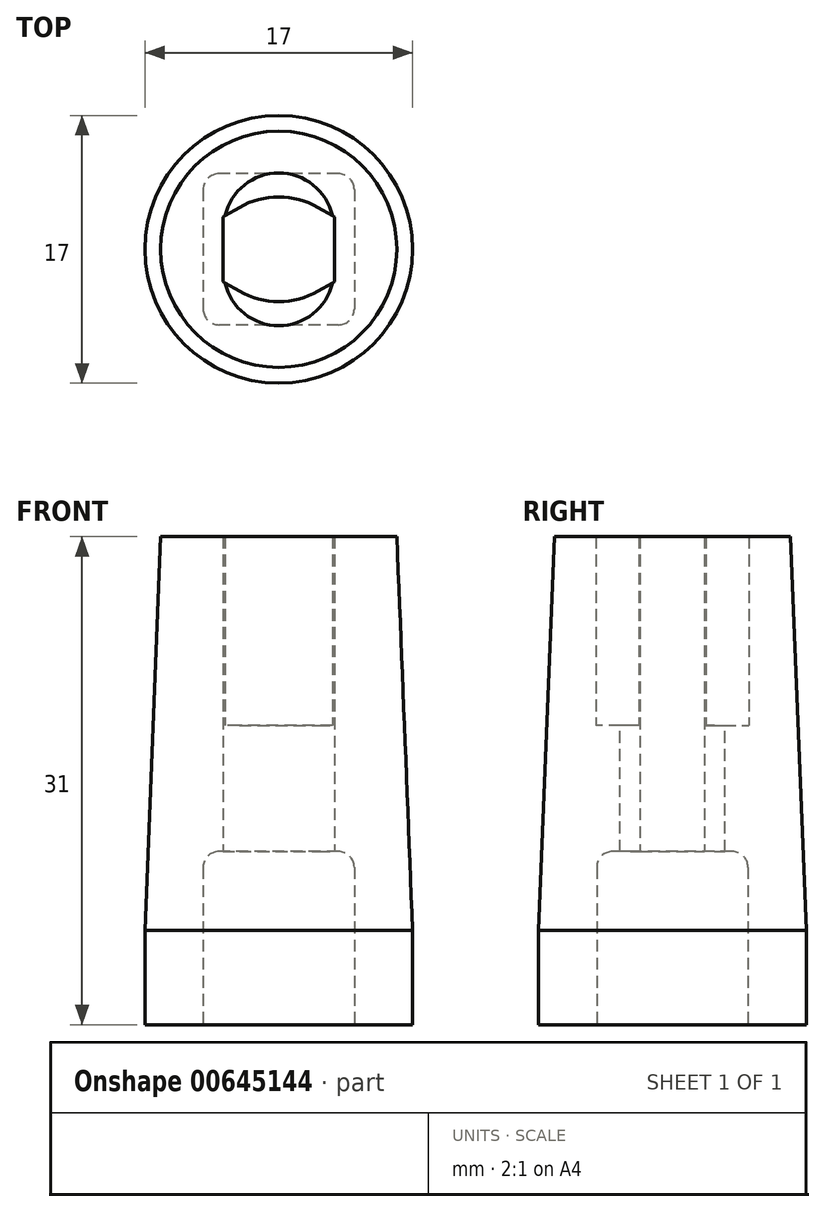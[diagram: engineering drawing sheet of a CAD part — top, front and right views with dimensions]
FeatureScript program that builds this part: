
annotation { "Feature Type Name" : "Feature", "Feature Type Description" : "" }
export const myFeature = defineFeature(function(context is Context, id is Id, definition is map)
    precondition{}
    {
        {
            var Q0;
            Q0=qCreatedBy(makeId("Top.planeOp"),FACE);
            var sketch = newSketch(context, id + "F0", { "sketchPlane" : qUnion([Q0])});
            skCircle(sketch, "E0.cCircle", {"center": v(0, 0) * mm, "radius": 3.55 * mm, "construction": true});
            skLineSegment(sketch, "E0.0", {"start": v(3.55, 2.05) * mm, "end": v(3.55, -2.05) * mm});
            skLineSegment(sketch, "E0.1", {"start": v(3.55, -2.05) * mm, "end": v(0, -4.1) * mm});
            skLineSegment(sketch, "E0.2", {"start": v(0, -4.1) * mm, "end": v(-3.55, -2.05) * mm});
            skLineSegment(sketch, "E0.3", {"start": v(-3.55, -2.05) * mm, "end": v(-3.55, 2.05) * mm});
            skLineSegment(sketch, "E0.4", {"start": v(-3.55, 2.05) * mm, "end": v(0, 4.1) * mm});
            skLineSegment(sketch, "E0.5", {"start": v(0, 4.1) * mm, "end": v(3.55, 2.05) * mm});
            skPoint(sketch, "E0.0.midPoint", {"position": v(3.55, 0) * mm});
            skLineSegment(sketch, "E1.bottom", {"start": v(3.5, 1.35) * mm, "end": v(-3.5, 1.35) * mm, "construction": true});
            skLineSegment(sketch, "E1.top", {"start": v(3.5, -1.35) * mm, "end": v(-3.5, -1.35) * mm, "construction": true});
            skLineSegment(sketch, "E1.left", {"start": v(3.5, 1.35) * mm, "end": v(3.5, -1.35) * mm});
            skLineSegment(sketch, "E1.right", {"start": v(-3.5, 1.35) * mm, "end": v(-3.5, -1.35) * mm});
            skArc(sketch, "E2", {"start": v(3.5, 1.35) * mm, "mid": v(0, 4.85) * mm, "end": v(-3.5, 1.35) * mm});
            skArc(sketch, "E3", {"start": v(-3.5, -1.35) * mm, "mid": v(0, -4.85) * mm, "end": v(3.5, -1.35) * mm});
            skCircle(sketch, "E4", {"center": v(0, 0) * mm, "radius": 8.5 * mm});
            skSolve(sketch);
        }
        {
            var Q0;
            {var subQ5=sQuery(id+"F0.wireOp",EDGE,"E0.0");Q0=makeQuery(id+"F0.imprint","IMPRINT",FACE,{"disambiguationData":[TD([[makeQuery(id+"F0.imprint","IMPRINT",EDGE,{"derivedFrom":subQ5}),1.0]])]});}
            extrude(context, id + "F1", {"entities" : qUnion([Q0]), "depth" : 16 * mm, "offsetDistance" : 25 * mm});
        }
        {
            var Q0;
            {var subQ0=sQuery(id+"F0.wireOp",EDGE,"E0.5");var subQ1=sQuery(id+"F0.wireOp",EDGE,"E0.4");var subQ2=makeQuery(id+"F0.imprint","INTERSECT",VERTEX,{"derivedFrom":[subQ1,subQ0]});Q0=makeQuery(id+"F0.imprint","IMPRINT",FACE,{"disambiguationData":[TD([[makeQuery(id+"F0.imprint","IMPRINT",EDGE,{"disambiguationData":[TD([[subQ2,1.0]])],"derivedFrom":subQ1}),1.0]])]});}
            var Q1;
            {var subQ0=sQuery(id+"F0.wireOp",EDGE,"E0.2");var subQ1=sQuery(id+"F0.wireOp",EDGE,"E0.1");var subQ2=makeQuery(id+"F0.imprint","INTERSECT",VERTEX,{"derivedFrom":[subQ1,subQ0]});Q1=makeQuery(id+"F0.imprint","IMPRINT",FACE,{"disambiguationData":[TD([[makeQuery(id+"F0.imprint","IMPRINT",EDGE,{"disambiguationData":[TD([[subQ2,1.0]])],"derivedFrom":subQ1}),1.0]])]});}
            extrude(context, id + "F2", {"entities" : qUnion([Q0, Q1]), "operationType" : NewBodyOperationType.ADD, "depth" : 4 * mm, "offsetDistance" : 25 * mm});
        }
        {
            var Q0;
            {var subQ5=sQuery(id+"F0.wireOp",EDGE,"E0.0");Q0=makeQuery(id+"F0.imprint","IMPRINT",FACE,{"disambiguationData":[TD([[makeQuery(id+"F0.imprint","IMPRINT",EDGE,{"derivedFrom":subQ5}),1.0]])]});}
            var Q1;
            {var subQ2=sQuery(id+"F0.wireOp",EDGE,"E0.3");Q1=makeQuery(id+"F0.imprint","IMPRINT",FACE,{"disambiguationData":[TD([[makeQuery(id+"F0.imprint","IMPRINT",EDGE,{"derivedFrom":subQ2}),-1.0]])]});}
            var Q2;
            {var subQ0=sQuery(id+"F0.wireOp",EDGE,"E0.5");var subQ1=sQuery(id+"F0.wireOp",EDGE,"E0.4");var subQ2=makeQuery(id+"F0.imprint","INTERSECT",VERTEX,{"derivedFrom":[subQ1,subQ0]});Q2=makeQuery(id+"F0.imprint","IMPRINT",FACE,{"disambiguationData":[TD([[makeQuery(id+"F0.imprint","IMPRINT",EDGE,{"disambiguationData":[TD([[subQ2,1.0]])],"derivedFrom":subQ1}),1.0]])]});}
            var Q3;
            {var subQ0=sQuery(id+"F0.wireOp",EDGE,"E0.2");var subQ1=sQuery(id+"F0.wireOp",EDGE,"E0.1");var subQ2=makeQuery(id+"F0.imprint","INTERSECT",VERTEX,{"derivedFrom":[subQ1,subQ0]});Q3=makeQuery(id+"F0.imprint","IMPRINT",FACE,{"disambiguationData":[TD([[makeQuery(id+"F0.imprint","IMPRINT",EDGE,{"disambiguationData":[TD([[subQ2,1.0]])],"derivedFrom":subQ1}),1.0]])]});}
            var Q4;
            {var subQ1=sQuery(id+"F0.wireOp",EDGE,"E0.0");Q4=makeQuery(id+"F0.imprint","IMPRINT",FACE,{"disambiguationData":[TD([[makeQuery(id+"F0.imprint","IMPRINT",EDGE,{"derivedFrom":subQ1}),-1.0]])]});}
            extrude(context, id + "F3", {"entities" : qUnion([Q0, Q1, Q2, Q3, Q4]), "operationType" : NewBodyOperationType.ADD, "oppositeDirection" : true, "depth" : 15 * mm, "offsetDistance" : 25 * mm});
        }
        {
            var Q0;
            Q0=makeQuery(id+"F3.opExtrude","CAP_FACE",FACE,{"disambiguationData":[OSD([sQuery(id+"F0.wireOp",EDGE,"E4")])],"isStart":false});
            var sketch = newSketch(context, id + "F4", { "sketchPlane" : qUnion([Q0])});
            skLineSegment(sketch, "E5.bottom", {"start": v(4.8, -4.8) * mm, "end": v(-4.8, -4.8) * mm});
            skLineSegment(sketch, "E5.top", {"start": v(4.8, 4.8) * mm, "end": v(-4.8, 4.8) * mm});
            skLineSegment(sketch, "E5.left", {"start": v(4.8, -4.8) * mm, "end": v(4.8, 4.8) * mm});
            skLineSegment(sketch, "E5.right", {"start": v(-4.8, -4.8) * mm, "end": v(-4.8, 4.8) * mm});
            skPoint(sketch, "E5.middle", {"position": v(0, 0) * mm});
            skSolve(sketch);
        }
        {
            var Q0;
            Q0=makeQuery(id+"F4.imprint","IMPRINT",FACE,{"disambiguationData":[TD([[makeQuery(id+"F4.imprint","IMPRINT",EDGE,{"derivedFrom":sQuery(id+"F4.wireOp",EDGE,"E5.bottom")}),-1.0]])]});
            extrude(context, id + "F5", {"entities" : qUnion([Q0]), "operationType" : NewBodyOperationType.REMOVE, "oppositeDirection" : true, "depth" : 11 * mm, "offsetDistance" : 25 * mm});
        }
        {
            var Q0;
            Q0=makeQuery(id+"F5.boolean.opBoolean","COPY",EDGE,{"derivedFrom":makeQuery(id+"F5.opExtrude","SWEPT_EDGE",EDGE,{"disambiguationData":[OSD([sQuery(id+"F4.wireOp",EDGE,"E5.top"),sQuery(id+"F4.wireOp",EDGE,"E5.right")])]})});
            var Q1;
            Q1=makeQuery(id+"F5.boolean.opBoolean","COPY",EDGE,{"derivedFrom":makeQuery(id+"F5.opExtrude","SWEPT_EDGE",EDGE,{"disambiguationData":[OSD([sQuery(id+"F4.wireOp",EDGE,"E5.bottom"),sQuery(id+"F4.wireOp",EDGE,"E5.right")])]})});
            var Q2;
            Q2=makeQuery(id+"F5.boolean.opBoolean","COPY",EDGE,{"derivedFrom":makeQuery(id+"F5.opExtrude","SWEPT_EDGE",EDGE,{"disambiguationData":[OSD([sQuery(id+"F4.wireOp",EDGE,"E5.top"),sQuery(id+"F4.wireOp",EDGE,"E5.left")])]})});
            var Q3;
            Q3=makeQuery(id+"F5.boolean.opBoolean","COPY",EDGE,{"derivedFrom":makeQuery(id+"F5.opExtrude","SWEPT_EDGE",EDGE,{"disambiguationData":[OSD([sQuery(id+"F4.wireOp",EDGE,"E5.bottom"),sQuery(id+"F4.wireOp",EDGE,"E5.left")])]})});
            var Q4;
            Q4=makeQuery(id+"F5.boolean.opBoolean","COPY",EDGE,{"derivedFrom":makeQuery(id+"F5.opExtrude","CAP_EDGE",EDGE,{"disambiguationData":[OSD([sQuery(id+"F4.wireOp",EDGE,"E5.bottom")])],"isStart":false})});
            var Q5;
            Q5=makeQuery(id+"F5.boolean.opBoolean","COPY",EDGE,{"derivedFrom":makeQuery(id+"F5.opExtrude","CAP_EDGE",EDGE,{"disambiguationData":[OSD([sQuery(id+"F4.wireOp",EDGE,"E5.right")])],"isStart":false})});
            var Q6;
            Q6=makeQuery(id+"F5.boolean.opBoolean","COPY",EDGE,{"derivedFrom":makeQuery(id+"F5.opExtrude","CAP_EDGE",EDGE,{"disambiguationData":[OSD([sQuery(id+"F4.wireOp",EDGE,"E5.top")])],"isStart":false})});
            var Q7;
            Q7=makeQuery(id+"F5.boolean.opBoolean","COPY",EDGE,{"derivedFrom":makeQuery(id+"F5.opExtrude","CAP_EDGE",EDGE,{"disambiguationData":[OSD([sQuery(id+"F4.wireOp",EDGE,"E5.left")])],"isStart":false})});
            fillet(context, id + "F6", {"entities" : qUnion([Q0, Q1, Q2, Q3, Q4, Q5, Q6, Q7]), "radius" : 1 * mm, "tangentPropagation" : true, "allowEdgeOverflow" : false});
        }
        {
            var Q0;
            Q0=makeQuery(id+"F1.opExtrude","CAP_EDGE",EDGE,{"disambiguationData":[OSD([sQuery(id+"F0.wireOp",EDGE,"E4")])],"isStart":false});
            chamfer(context, id + "F7", {"entities" : qUnion([Q0]), "chamferType" : ChamferType.TWO_OFFSETS, "width1" : 1 * mm, "oppositeDirection" : false, "width2" : 25 * mm, "tangentPropagation" : true});
        }
        {
            var Q0;
            {var subQ0=sQuery(id+"F0.wireOp",EDGE,"E0.2");var subQ1=sQuery(id+"F0.wireOp",EDGE,"E0.1");Q0=makeQuery(id+"F3.boolean.opBoolean","MERGE",EDGE,{"derivedFrom":[makeQuery(id+"F2.opExtrude","SWEPT_EDGE",EDGE,{"disambiguationData":[OSD([subQ1,subQ0])]}),makeQuery(id+"F3.opExtrude","SWEPT_EDGE",EDGE,{"disambiguationData":[OSD([subQ1,subQ0])]})]});}
            var Q1;
            {var subQ0=sQuery(id+"F0.wireOp",EDGE,"E0.5");var subQ1=sQuery(id+"F0.wireOp",EDGE,"E0.4");Q1=makeQuery(id+"F3.boolean.opBoolean","MERGE",EDGE,{"derivedFrom":[makeQuery(id+"F2.opExtrude","SWEPT_EDGE",EDGE,{"disambiguationData":[OSD([subQ1,subQ0])]}),makeQuery(id+"F3.opExtrude","SWEPT_EDGE",EDGE,{"disambiguationData":[OSD([subQ1,subQ0])]})]});}
            fillet(context, id + "F8", {"entities" : qUnion([Q0, Q1]), "tangentPropagation" : true, "radius" : 5 * mm, "defaultsChanged" : false, "vertexSettings" : [], "allowEdgeOverflow" : false});
        }
        {
            var Q0;
            {var subQ0=sQuery(id+"F0.wireOp",EDGE,"E0.1");var subQ1=sQuery(id+"F0.wireOp",EDGE,"E0.5");var subQ2=sQuery(id+"F0.wireOp",EDGE,"E1.left");var subQ3=sQuery(id+"F0.wireOp",EDGE,"E3");var subQ4=sQuery(id+"F0.wireOp",EDGE,"E2");Q0=makeQuery(id+"F3.boolean.opBoolean","SPLIT",FACE,{"disambiguationData":[TD([makeQuery(id+"F1.opExtrude","SWEPT_FACE",FACE,{"disambiguationData":[OSD([sQuery(id+"F0.wireOp",EDGE,"E0.0")])]})])],"derivedFrom":makeQuery(id+"F3.opExtrude","CAP_FACE",FACE,{"disambiguationData":[OSD([subQ0,sQuery(id+"F0.wireOp",EDGE,"E0.2"),sQuery(id+"F0.wireOp",EDGE,"E0.4"),subQ1,subQ2,sQuery(id+"F0.wireOp",EDGE,"E1.right"),subQ4,subQ3,sQuery(id+"F0.wireOp",EDGE,"E4")])],"isStart":true})});}
            var Q1;
            {var subQ0=sQuery(id+"F0.wireOp",EDGE,"E0.4");var subQ1=sQuery(id+"F0.wireOp",EDGE,"E0.2");var subQ2=sQuery(id+"F0.wireOp",EDGE,"E1.right");var subQ3=sQuery(id+"F0.wireOp",EDGE,"E2");var subQ4=sQuery(id+"F0.wireOp",EDGE,"E3");Q1=makeQuery(id+"F3.boolean.opBoolean","SPLIT",FACE,{"disambiguationData":[TD([makeQuery(id+"F1.opExtrude","SWEPT_FACE",FACE,{"disambiguationData":[OSD([subQ1])]})])],"derivedFrom":makeQuery(id+"F3.opExtrude","CAP_FACE",FACE,{"disambiguationData":[OSD([sQuery(id+"F0.wireOp",EDGE,"E0.1"),subQ1,subQ0,sQuery(id+"F0.wireOp",EDGE,"E0.5"),sQuery(id+"F0.wireOp",EDGE,"E1.left"),subQ2,subQ3,subQ4,sQuery(id+"F0.wireOp",EDGE,"E4")])],"isStart":true})});}
            extrude(context, id + "F9", {"entities" : qUnion([Q0, Q1]), "operationType" : NewBodyOperationType.REMOVE, "oppositeDirection" : true, "depth" : 25 * mm, "offsetDistance" : 25 * mm});
        }
    });
